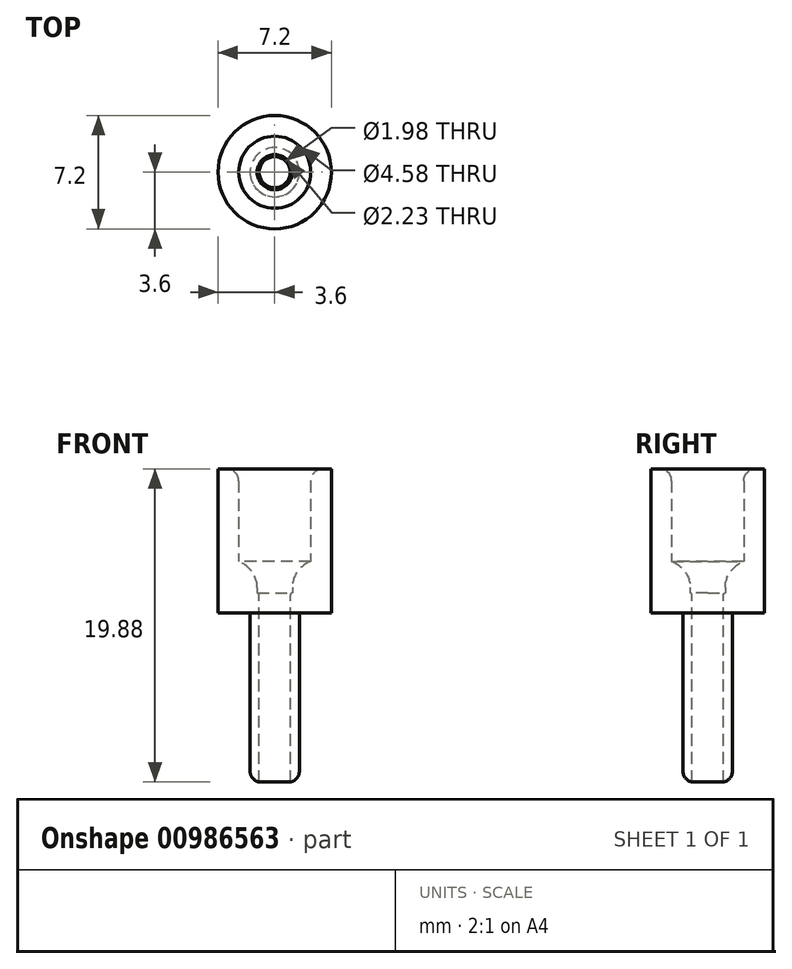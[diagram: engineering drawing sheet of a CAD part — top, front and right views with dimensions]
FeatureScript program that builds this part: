
annotation { "Feature Type Name" : "Feature", "Feature Type Description" : "" }
export const myFeature = defineFeature(function(context is Context, id is Id, definition is map)
    precondition{}
    {
        {
            var Q0;
            Q0=qCreatedBy(makeId("Top.planeOp"),FACE);
            var sketch = newSketch(context, id + "F0", { "sketchPlane" : qUnion([Q0])});
            skCircle(sketch, "E0", {"center": v(0, 0) * mm, "radius": 1.56 * mm});
            skCircle(sketch, "E1", {"center": v(0, 0) * mm, "radius": 0.99 * mm});
            skSolve(sketch);
        }
        {
            var Q0;
            Q0=makeQuery(id+"F0.imprint","IMPRINT",FACE,{"disambiguationData":[TD([[makeQuery(id+"F0.imprint","IMPRINT",EDGE,{"derivedFrom":sQuery(id+"F0.wireOp",EDGE,"E0")}),1.0]])]});
            extrude(context, id + "F1", {"entities" : qUnion([Q0]), "oppositeDirection" : true, "depth" : 12 * mm, "offsetDistance" : 25 * mm});
        }
        {
            var Q0;
            Q0=makeQuery(id+"F1.opExtrude","CAP_FACE",FACE,{"disambiguationData":[OSD([sQuery(id+"F0.wireOp",EDGE,"E0"),sQuery(id+"F0.wireOp",EDGE,"E1")])],"isStart":true});
            var sketch = newSketch(context, id + "F2", { "sketchPlane" : qUnion([Q0])});
            skCircle(sketch, "E2", {"center": v(0, 0) * mm, "radius": 2.5 * mm});
            skCircle(sketch, "E3", {"center": v(0, 0) * mm, "radius": 3.6 * mm});
            skSolve(sketch);
        }
        {
            var Q0;
            Q0=makeQuery(id+"F2.imprint","IMPRINT",FACE,{"disambiguationData":[TD([[makeQuery(id+"F2.imprint","IMPRINT",EDGE,{"derivedFrom":sQuery(id+"F2.wireOp",EDGE,"E2")}),-1.0]])]});
            var Q1;
            Q1=makeQuery(id+"F2.imprint","IMPRINT",FACE,{"disambiguationData":[TD([[makeQuery(id+"F2.imprint","IMPRINT",EDGE,{"derivedFrom":sQuery(id+"F2.wireOp",EDGE,"E2")}),1.0]])]});
            extrude(context, id + "F3", {"entities" : qUnion([Q0, Q1]), "operationType" : NewBodyOperationType.ADD, "oppositeDirection" : true, "depth" : 1.27 * mm, "offsetDistance" : 25 * mm});
        }
        {
            var Q0;
            {var subQ0=sQuery(id+"F0.wireOp",EDGE,"E0");Q0=makeQuery(id+"F3.boolean.opBoolean","MERGE",FACE,{"derivedFrom":[makeQuery(id+"F1.opExtrude","CAP_FACE",FACE,{"disambiguationData":[OSD([subQ0,sQuery(id+"F0.wireOp",EDGE,"E1")])],"isStart":true}),makeQuery(id+"F3.opExtrude","CAP_FACE",FACE,{"disambiguationData":[OSD([subQ0,sQuery(id+"F2.wireOp",EDGE,"E3")])],"isStart":true})]});}
            var sketch = newSketch(context, id + "F4", { "sketchPlane" : qUnion([Q0])});
            skCircle(sketch, "E4", {"center": v(0, 0) * mm, "radius": 2.29 * mm});
            skCircle(sketch, "E5.0", {"center": v(0, 0) * mm, "radius": 3.6 * mm});
            skSolve(sketch);
        }
        {
            var Q0;
            Q0 = qSketchRegion(id + "F4", true);
            extrude(context, id + "F5", {"entities" : qUnion([Q0]), "depth" : 7.88 * mm, "offsetDistance" : 25 * mm});
        }
        {
            var Q0;
            Q0=makeQuery(id+"F5.opExtrude","CAP_FACE",FACE,{"disambiguationData":[OSD([sQuery(id+"F4.wireOp",EDGE,"E4"),sQuery(id+"F4.wireOp",EDGE,"E5.0")])],"isStart":true});
            var sketch = newSketch(context, id + "F6", { "sketchPlane" : qUnion([Q0])});
            skCircle(sketch, "E6.0", {"center": v(0, 0) * mm, "radius": 0.99 * mm, "construction": true});
            skCircle(sketch, "E7", {"center": v(0, 0) * mm, "radius": 1.12 * mm});
            skSolve(sketch);
        }
        {
            var Q0;
            Q0=makeQuery(id+"F6.imprint","IMPRINT",FACE,{"disambiguationData":[TD([[makeQuery(id+"F6.imprint","IMPRINT",EDGE,{"derivedFrom":sQuery(id+"F6.wireOp",EDGE,"E7")}),-1.0]])]});
            extrude(context, id + "F7", {"entities" : qUnion([Q0]), "operationType" : NewBodyOperationType.ADD, "oppositeDirection" : true, "depth" : 2 * mm, "offsetDistance" : 25 * mm});
        }
        {
            var Q0;
            Q0=makeQuery(id+"F7.opExtrude","CAP_EDGE",EDGE,{"disambiguationData":[OSD([sQuery(id+"F6.wireOp",EDGE,"E7")])],"isStart":false});
            fillet(context, id + "F8", {"entities" : qUnion([Q0]), "radius" : 1.75 * mm, "tangentPropagation" : true, "allowEdgeOverflow" : false});
        }
        {
            var Q0;
            Q0=makeQuery(id+"F5.opExtrude","CAP_EDGE",EDGE,{"disambiguationData":[OSD([sQuery(id+"F4.wireOp",EDGE,"E4")])],"isStart":false});
            fillet(context, id + "F9", {"entities" : qUnion([Q0]), "radius" : 0.75 * mm, "tangentPropagation" : true, "allowEdgeOverflow" : false});
        }
        {
            var Q0;
            Q0=makeQuery(id+"F1.opExtrude","CAP_EDGE",EDGE,{"disambiguationData":[OSD([sQuery(id+"F0.wireOp",EDGE,"E0")])],"isStart":false});
            fillet(context, id + "F10", {"entities" : qUnion([Q0]), "radius" : 0.68 * mm, "tangentPropagation" : true, "allowEdgeOverflow" : false});
        }
        {
            var Q0;
            Q0=makeQuery(id+"F1.opExtrude","CAP_EDGE",EDGE,{"disambiguationData":[OSD([sQuery(id+"F0.wireOp",EDGE,"E1")])],"isStart":true});
            fillet(context, id + "F11", {"entities" : qUnion([Q0]), "radius" : 0.13 * mm, "tangentPropagation" : true, "allowEdgeOverflow" : false});
        }
    });
